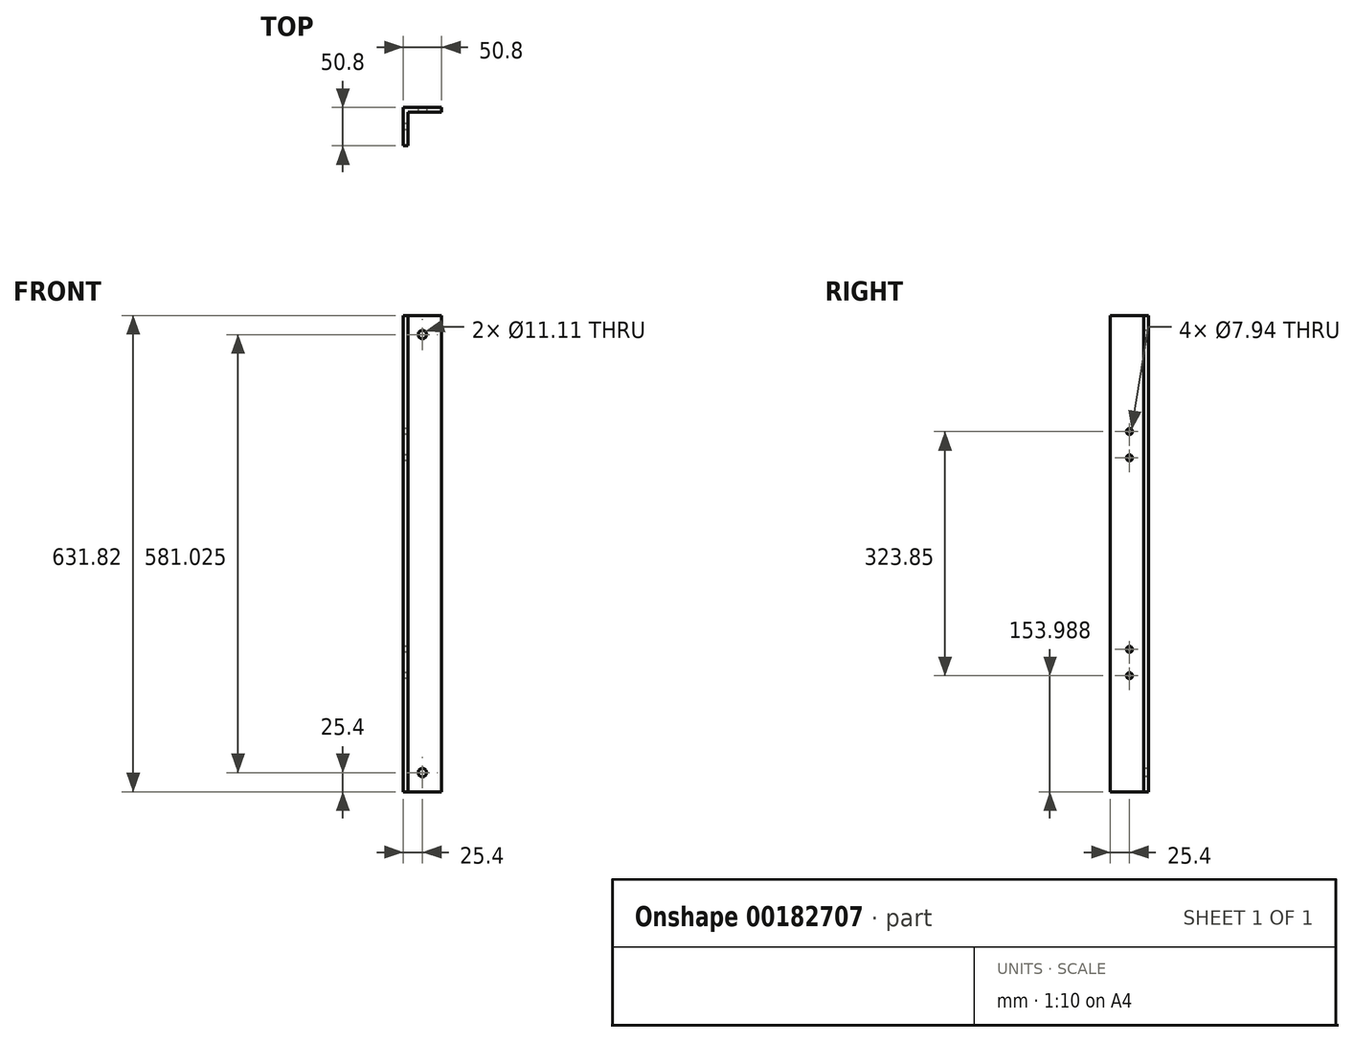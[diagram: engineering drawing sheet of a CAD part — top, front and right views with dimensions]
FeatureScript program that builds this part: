
annotation { "Feature Type Name" : "Feature", "Feature Type Description" : "" }
export const myFeature = defineFeature(function(context is Context, id is Id, definition is map)
    precondition{}
    {
        {
            var Q0;
            Q0=qCreatedBy(makeId("Top.planeOp"),FACE);
            var sketch = newSketch(context, id + "F0", { "sketchPlane" : qUnion([Q0])});
            skLineSegment(sketch, "E0", {"start": v(0, 0) * mm, "end": v(50.8, 0) * mm});
            skLineSegment(sketch, "E1", {"start": v(0, 0) * mm, "end": v(0, -50.8) * mm});
            skLineSegment(sketch, "E2", {"start": v(0, -50.8) * mm, "end": v(6.35, -50.8) * mm});
            skLineSegment(sketch, "E3", {"start": v(6.35, -6.35) * mm, "end": v(50.8, -6.35) * mm});
            skLineSegment(sketch, "E4", {"start": v(50.8, -6.35) * mm, "end": v(50.8, 0) * mm});
            skLineSegment(sketch, "E5", {"start": v(6.35, -6.35) * mm, "end": v(6.35, -50.8) * mm});
            skSolve(sketch);
        }
        {
            var Q0;
            Q0=makeQuery(id+"F0.imprint","IMPRINT",FACE,{"disambiguationData":[TD([[makeQuery(id+"F0.imprint","IMPRINT",EDGE,{"derivedFrom":sQuery(id+"F0.wireOp",EDGE,"E0")}),-1.0]])]});
            extrude(context, id + "F1", {"entities" : qUnion([Q0]), "depth" : 631.82 * mm});
        }
        {
            var Q0;
            Q0=makeQuery(id+"F1.opExtrude","SWEPT_FACE",FACE,{"disambiguationData":[OSD([sQuery(id+"F0.wireOp",EDGE,"E3")])]});
            var sketch = newSketch(context, id + "F2", { "sketchPlane" : qUnion([Q0])});
            skCircle(sketch, "E6", {"center": v(25.4, 606.43) * mm, "radius": 5.56 * mm});
            skCircle(sketch, "E7", {"center": v(25.4, 25.4) * mm, "radius": 5.56 * mm});
            skSolve(sketch);
        }
        {
            var Q0;
            Q0=makeQuery(id+"F2.imprint","IMPRINT",FACE,{"disambiguationData":[TD([[makeQuery(id+"F2.imprint","IMPRINT",EDGE,{"derivedFrom":sQuery(id+"F2.wireOp",EDGE,"E6")}),1.0]])]});
            var Q1;
            Q1=makeQuery(id+"F2.imprint","IMPRINT",FACE,{"disambiguationData":[TD([[makeQuery(id+"F2.imprint","IMPRINT",EDGE,{"derivedFrom":sQuery(id+"F2.wireOp",EDGE,"E7")}),1.0]])]});
            extrude(context, id + "F3", {"entities" : qUnion([Q0, Q1]), "operationType" : NewBodyOperationType.REMOVE, "endBound" : BoundingType.THROUGH_ALL, "oppositeDirection" : true, "depth" : 25.4 * mm});
        }
        {
            var Q0;
            Q0=makeQuery(id+"F1.opExtrude","SWEPT_FACE",FACE,{"disambiguationData":[OSD([sQuery(id+"F0.wireOp",EDGE,"E1")])]});
            var sketch = newSketch(context, id + "F4", { "sketchPlane" : qUnion([Q0])});
            skCircle(sketch, "E8", {"center": v(25.4, 477.84) * mm, "radius": 3.97 * mm});
            skCircle(sketch, "E9", {"center": v(25.4, 442.91) * mm, "radius": 3.97 * mm});
            skCircle(sketch, "E10", {"center": v(25.4, 188.91) * mm, "radius": 3.97 * mm});
            skCircle(sketch, "E11", {"center": v(25.4, 153.99) * mm, "radius": 3.97 * mm});
            skSolve(sketch);
        }
        {
            var Q0;
            Q0=makeQuery(id+"F4.imprint","IMPRINT",FACE,{"disambiguationData":[TD([[makeQuery(id+"F4.imprint","IMPRINT",EDGE,{"derivedFrom":sQuery(id+"F4.wireOp",EDGE,"E8")}),1.0]])]});
            var Q1;
            Q1=makeQuery(id+"F4.imprint","IMPRINT",FACE,{"disambiguationData":[TD([[makeQuery(id+"F4.imprint","IMPRINT",EDGE,{"derivedFrom":sQuery(id+"F4.wireOp",EDGE,"E11")}),1.0]])]});
            var Q2;
            Q2=makeQuery(id+"F4.imprint","IMPRINT",FACE,{"disambiguationData":[TD([[makeQuery(id+"F4.imprint","IMPRINT",EDGE,{"derivedFrom":sQuery(id+"F4.wireOp",EDGE,"E10")}),1.0]])]});
            var Q3;
            Q3=makeQuery(id+"F4.imprint","IMPRINT",FACE,{"disambiguationData":[TD([[makeQuery(id+"F4.imprint","IMPRINT",EDGE,{"derivedFrom":sQuery(id+"F4.wireOp",EDGE,"E9")}),1.0]])]});
            extrude(context, id + "F5", {"entities" : qUnion([Q0, Q1, Q2, Q3]), "operationType" : NewBodyOperationType.REMOVE, "endBound" : BoundingType.THROUGH_ALL, "oppositeDirection" : true, "depth" : 25.4 * mm});
        }
    });
